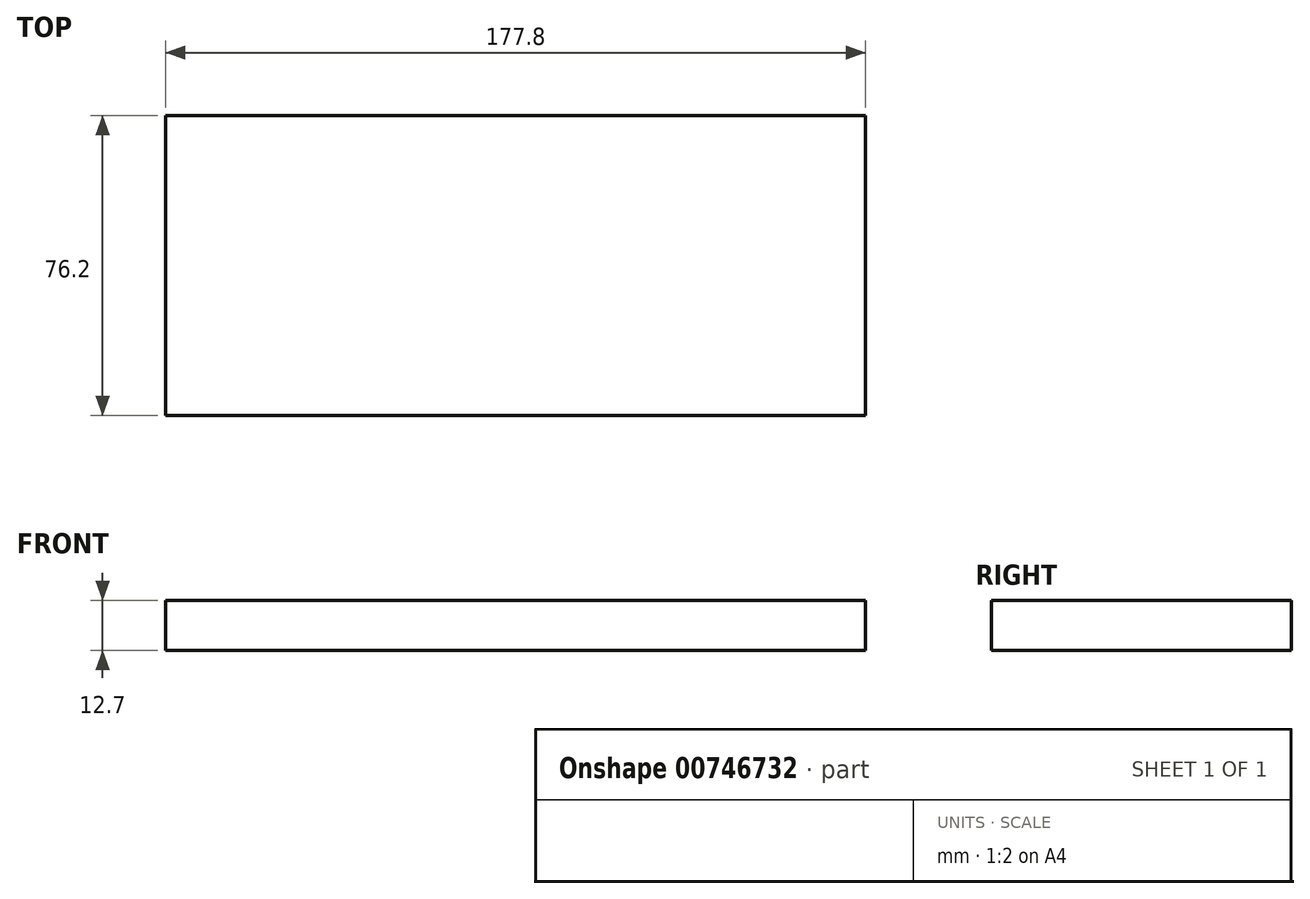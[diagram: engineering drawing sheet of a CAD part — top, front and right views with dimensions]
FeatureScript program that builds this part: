
annotation { "Feature Type Name" : "Feature", "Feature Type Description" : "" }
export const myFeature = defineFeature(function(context is Context, id is Id, definition is map)
    precondition{}
    {
        {
            var Q0;
            Q0=qCreatedBy(makeId("Top.planeOp"),FACE);
            var sketch = newSketch(context, id + "F0", { "sketchPlane" : qUnion([Q0])});
            skLineSegment(sketch, "E0.bottom", {"start": v(-84.1, 23.18) * mm, "end": v(93.7, 23.18) * mm});
            skLineSegment(sketch, "E0.top", {"start": v(-84.1, -53.02) * mm, "end": v(93.7, -53.02) * mm});
            skLineSegment(sketch, "E0.left", {"start": v(-84.1, 23.18) * mm, "end": v(-84.1, -53.02) * mm});
            skLineSegment(sketch, "E0.right", {"start": v(93.7, 23.18) * mm, "end": v(93.7, -53.02) * mm});
            skSolve(sketch);
        }
        {
            var Q0;
            Q0 = qSketchRegion(id + "F0", true);
            extrude(context, id + "F1", {"entities" : qUnion([Q0]), "depth" : 12.7 * mm, "offsetDistance" : 25.4 * mm});
        }
    });
